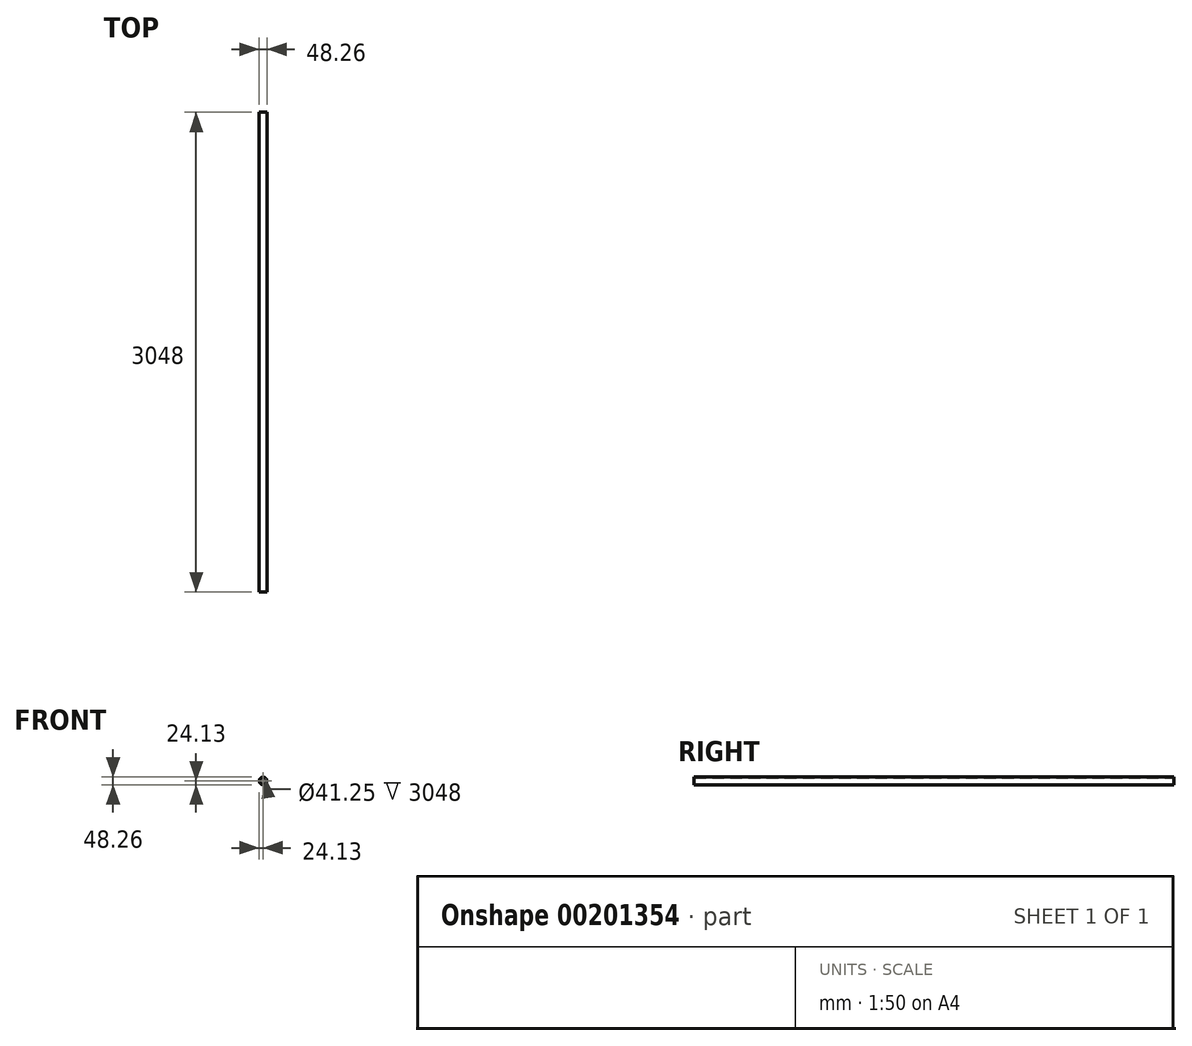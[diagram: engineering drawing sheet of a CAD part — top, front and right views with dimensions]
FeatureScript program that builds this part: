
annotation { "Feature Type Name" : "Feature", "Feature Type Description" : "" }
export const myFeature = defineFeature(function(context is Context, id is Id, definition is map)
    precondition{}
    {
        {
            var Q0;
            Q0=qCreatedBy(makeId("Front.planeOp"),FACE);
            var sketch = newSketch(context, id + "F0", { "sketchPlane" : qUnion([Q0])});
            skCircle(sketch, "E0", {"center": v(0, 0) * mm, "radius": 24.13 * mm});
            skCircle(sketch, "E1", {"center": v(0, 0) * mm, "radius": 20.62 * mm});
            skSolve(sketch);
        }
        {
            var Q0;
            Q0 = qSketchRegion(id + "F0", true);
            extrude(context, id + "F1", {"entities" : qUnion([Q0]), "depth" : 3048 * mm});
        }
    });
